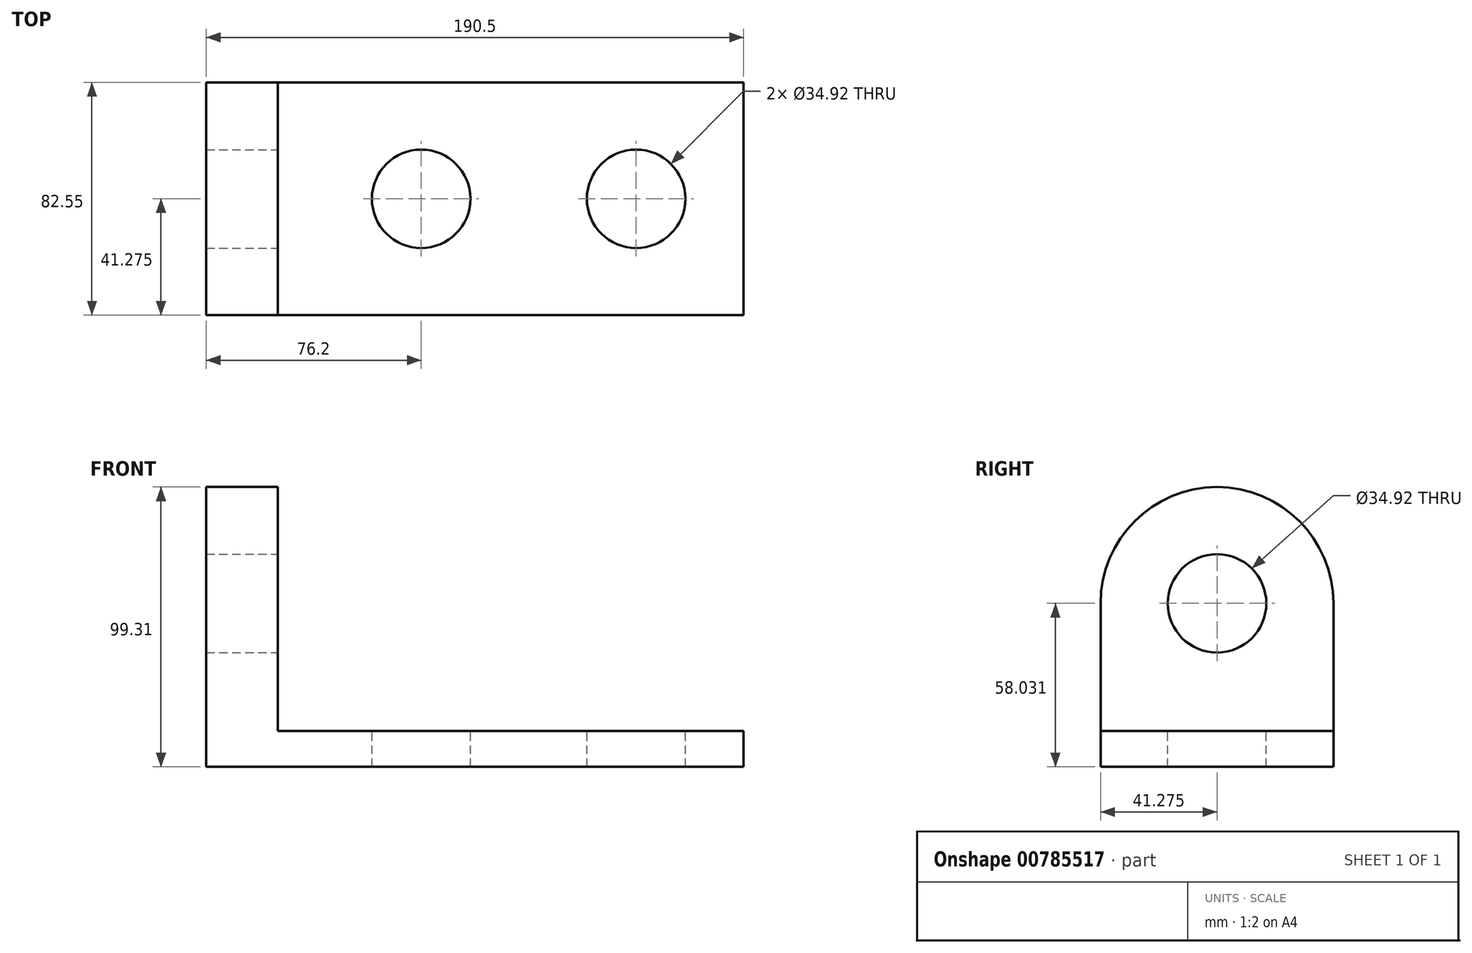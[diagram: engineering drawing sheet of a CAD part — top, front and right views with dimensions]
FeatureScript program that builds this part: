
annotation { "Feature Type Name" : "Feature", "Feature Type Description" : "" }
export const myFeature = defineFeature(function(context is Context, id is Id, definition is map)
    precondition{}
    {
        {
            var Q0;
            Q0=qCreatedBy(makeId("Front.planeOp"),FACE);
            var sketch = newSketch(context, id + "F0", { "sketchPlane" : qUnion([Q0])});
            skLineSegment(sketch, "E0", {"start": v(0, 0) * mm, "end": v(190.5, 0) * mm});
            skLineSegment(sketch, "E1", {"start": v(190.5, 0) * mm, "end": v(190.5, 12.7) * mm});
            skLineSegment(sketch, "E2", {"start": v(190.5, 12.7) * mm, "end": v(25.4, 12.7) * mm});
            skLineSegment(sketch, "E3", {"start": v(25.4, 12.7) * mm, "end": v(25.4, 116.06) * mm});
            skLineSegment(sketch, "E4", {"start": v(25.4, 116.06) * mm, "end": v(0, 116.06) * mm});
            skLineSegment(sketch, "E5", {"start": v(0, 116.06) * mm, "end": v(0, 0) * mm});
            skSolve(sketch);
        }
        {
            var Q0;
            Q0 = qSketchRegion(id + "F0", true);
            extrude(context, id + "F1", {"entities" : qUnion([Q0]), "depth" : 82.55 * mm, "offsetDistance" : 25.4 * mm});
        }
        {
            var Q0;
            Q0=makeQuery(id+"F1.opExtrude","SWEPT_FACE",FACE,{"disambiguationData":[OSD([sQuery(id+"F0.wireOp",EDGE,"E2")])]});
            var sketch = newSketch(context, id + "F2", { "sketchPlane" : qUnion([Q0])});
            skLineSegment(sketch, "E6", {"start": v(190.5, -41.28) * mm, "end": v(152.4, -41.28) * mm, "construction": true});
            skLineSegment(sketch, "E7", {"start": v(152.4, -41.28) * mm, "end": v(76.2, -41.28) * mm, "construction": true});
            skCircle(sketch, "E8", {"center": v(76.2, -41.28) * mm, "radius": 17.46 * mm});
            skCircle(sketch, "E9", {"center": v(152.4, -41.28) * mm, "radius": 17.46 * mm});
            skSolve(sketch);
        }
        {
            var Q0;
            Q0 = qSketchRegion(id + "F2", true);
            extrude(context, id + "F3", {"entities" : qUnion([Q0]), "operationType" : NewBodyOperationType.REMOVE, "oppositeDirection" : true, "depth" : 12.7 * mm, "offsetDistance" : 25.4 * mm});
        }
        {
            var Q0;
            Q0=makeQuery(id+"F1.opExtrude","SWEPT_FACE",FACE,{"disambiguationData":[OSD([sQuery(id+"F0.wireOp",EDGE,"E5")])]});
            var sketch = newSketch(context, id + "F4", { "sketchPlane" : qUnion([Q0])});
            skLineSegment(sketch, "E10", {"start": v(0, 0) * mm, "end": v(0, 58.03) * mm, "construction": true});
            skArc(sketch, "E11", {"start": v(82.55, 58.03) * mm, "mid": v(41.28, 99.3) * mm, "end": v(0, 58.03) * mm});
            skSolve(sketch);
        }
        {
            var Q0;
            {var subQ0=sQuery(id+"F4.wireOp",EDGE,"E11");Q0=makeQuery(id+"F4.imprint","IMPRINT",FACE,{"disambiguationData":[TD([[makeQuery(id+"F4.imprint","IMPRINT",EDGE,{"derivedFrom":subQ0}),-1.0]])]});}
            extrude(context, id + "F5", {"entities" : qUnion([Q0]), "operationType" : NewBodyOperationType.REMOVE, "oppositeDirection" : true, "depth" : 25.4 * mm, "offsetDistance" : 25.4 * mm});
        }
        {
            var Q0;
            Q0=makeQuery(id+"F1.opExtrude","SWEPT_FACE",FACE,{"disambiguationData":[OSD([sQuery(id+"F0.wireOp",EDGE,"E3")])]});
            var sketch = newSketch(context, id + "F6", { "sketchPlane" : qUnion([Q0])});
            skCircle(sketch, "E12", {"center": v(-41.28, 58.03) * mm, "radius": 17.46 * mm});
            skSolve(sketch);
        }
        {
            var Q0;
            Q0 = qSketchRegion(id + "F6", true);
            extrude(context, id + "F7", {"entities" : qUnion([Q0]), "operationType" : NewBodyOperationType.REMOVE, "oppositeDirection" : true, "depth" : 25.4 * mm, "offsetDistance" : 25.4 * mm});
        }
    });
